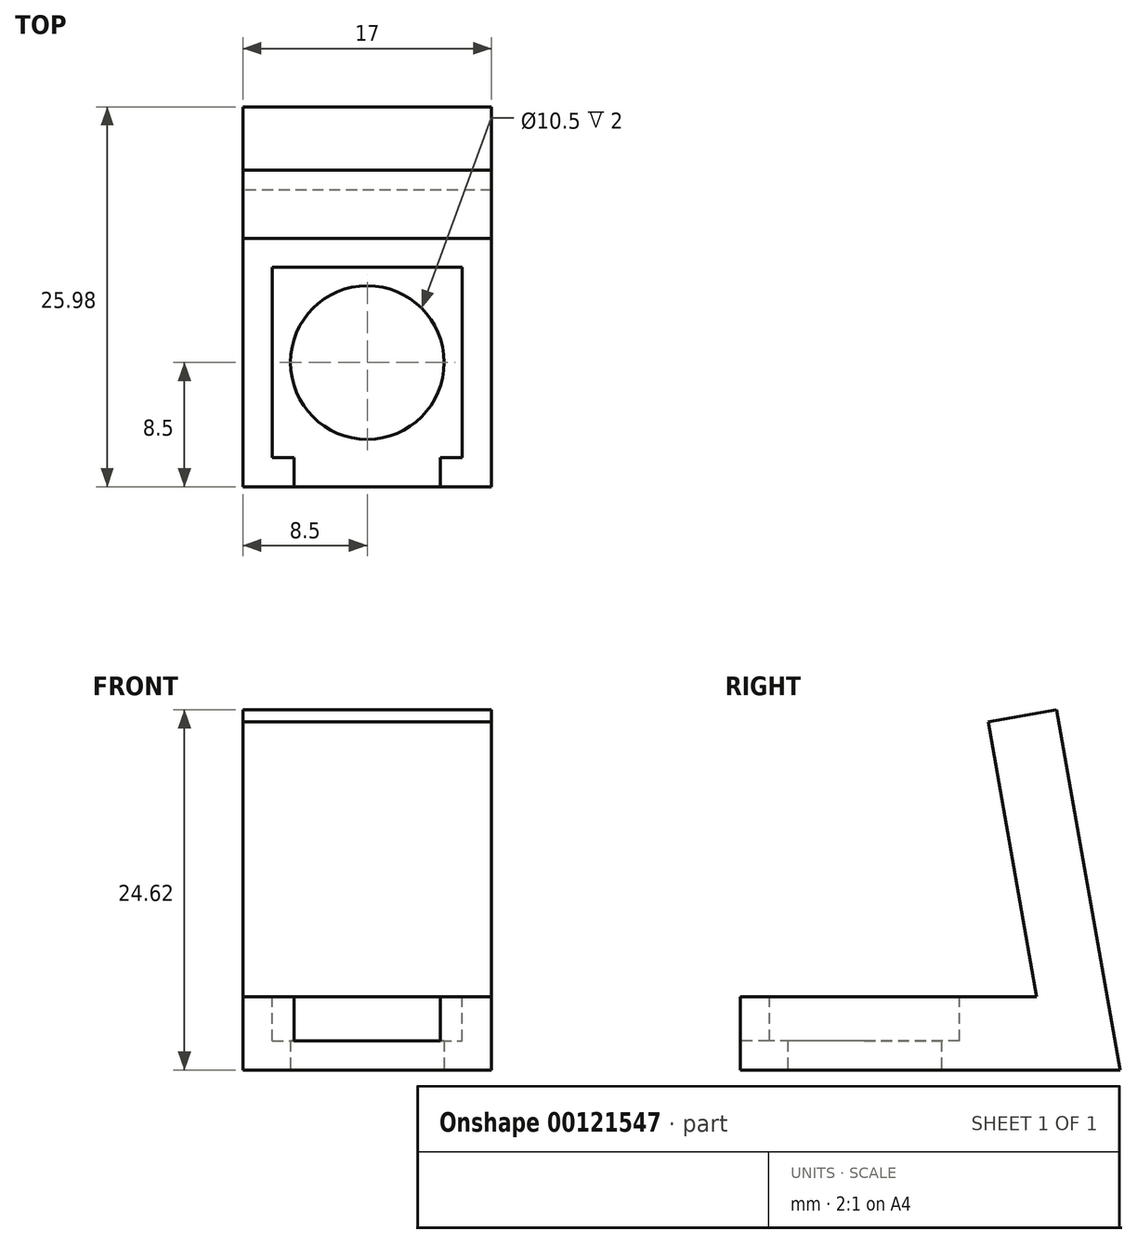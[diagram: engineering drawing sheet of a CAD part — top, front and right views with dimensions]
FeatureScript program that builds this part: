
annotation { "Feature Type Name" : "Feature", "Feature Type Description" : "" }
export const myFeature = defineFeature(function(context is Context, id is Id, definition is map)
    precondition{}
    {
        {
            var Q0;
            Q0=qCreatedBy(makeId("Top.planeOp"),FACE);
            var sketch = newSketch(context, id + "F0", { "sketchPlane" : qUnion([Q0])});
            skLineSegment(sketch, "E0.bottom", {"start": v(-8.5, 8.5) * mm, "end": v(8.5, 8.5) * mm});
            skLineSegment(sketch, "E0.top", {"start": v(-8.5, -8.5) * mm, "end": v(8.5, -8.5) * mm});
            skLineSegment(sketch, "E0.left", {"start": v(-8.5, 8.5) * mm, "end": v(-8.5, -8.5) * mm});
            skLineSegment(sketch, "E0.right", {"start": v(8.5, 8.5) * mm, "end": v(8.5, -8.5) * mm});
            skPoint(sketch, "E0.middle", {"position": v(0, 0) * mm});
            skSolve(sketch);
        }
        {
            var Q0;
            Q0=makeQuery(id+"F0.imprint","IMPRINT",FACE,{"disambiguationData":[TD([[makeQuery(id+"F0.imprint","IMPRINT",EDGE,{"derivedFrom":sQuery(id+"F0.wireOp",EDGE,"E0.bottom")}),-1.0]])]});
            extrude(context, id + "F1", {"entities" : qUnion([Q0]), "depth" : 5 * mm});
        }
        {
            var Q0;
            Q0=makeQuery(id+"F1.opExtrude","CAP_FACE",FACE,{"disambiguationData":[OSD([sQuery(id+"F0.wireOp",EDGE,"E0.bottom"),sQuery(id+"F0.wireOp",EDGE,"E0.top"),sQuery(id+"F0.wireOp",EDGE,"E0.left"),sQuery(id+"F0.wireOp",EDGE,"E0.right")])],"isStart":false});
            var sketch = newSketch(context, id + "F2", { "sketchPlane" : qUnion([Q0])});
            skLineSegment(sketch, "E1.bottom", {"start": v(-6.5, 6.5) * mm, "end": v(6.5, 6.5) * mm});
            skLineSegment(sketch, "E1.top", {"start": v(-6.5, -6.5) * mm, "end": v(-5, -6.5) * mm});
            skLineSegment(sketch, "E1.left", {"start": v(-6.5, 6.5) * mm, "end": v(-6.5, -6.5) * mm});
            skLineSegment(sketch, "E1.right", {"start": v(6.5, 6.5) * mm, "end": v(6.5, -6.5) * mm});
            skPoint(sketch, "E1.middle", {"position": v(0, 0) * mm});
            skLineSegment(sketch, "E2.top", {"start": v(-5, -11.8) * mm, "end": v(5, -11.8) * mm});
            skLineSegment(sketch, "E2.left", {"start": v(-5, -6.5) * mm, "end": v(-5, -11.8) * mm});
            skLineSegment(sketch, "E2.right", {"start": v(5, -6.5) * mm, "end": v(5, -11.8) * mm});
            skLineSegment(sketch, "E3.trimOffspring", {"start": v(5, -6.5) * mm, "end": v(6.5, -6.5) * mm});
            skSolve(sketch);
        }
        {
            var Q0;
            Q0=makeQuery(id+"F2.imprint","IMPRINT",FACE,{"disambiguationData":[TD([[makeQuery(id+"F2.imprint","IMPRINT",EDGE,{"derivedFrom":sQuery(id+"F2.wireOp",EDGE,"E1.bottom")}),-1.0]])]});
            extrude(context, id + "F3", {"entities" : qUnion([Q0]), "operationType" : NewBodyOperationType.REMOVE, "oppositeDirection" : true, "depth" : 3 * mm});
        }
        {
            var Q0;
            Q0=makeQuery(id+"F1.opExtrude","CAP_FACE",FACE,{"disambiguationData":[OSD([sQuery(id+"F0.wireOp",EDGE,"E0.bottom"),sQuery(id+"F0.wireOp",EDGE,"E0.top"),sQuery(id+"F0.wireOp",EDGE,"E0.left"),sQuery(id+"F0.wireOp",EDGE,"E0.right")])],"isStart":true});
            var sketch = newSketch(context, id + "F4", { "sketchPlane" : qUnion([Q0])});
            skCircle(sketch, "E4", {"center": v(0, 0) * mm, "radius": 5.25 * mm});
            skSolve(sketch);
        }
        {
            var Q0;
            Q0=makeQuery(id+"F4.imprint","IMPRINT",FACE,{"disambiguationData":[TD([[makeQuery(id+"F4.imprint","IMPRINT",EDGE,{"derivedFrom":sQuery(id+"F4.wireOp",EDGE,"E4")}),1.0]])]});
            extrude(context, id + "F5", {"entities" : qUnion([Q0]), "operationType" : NewBodyOperationType.REMOVE, "oppositeDirection" : true, "depth" : 25 * mm});
        }
        {
            var Q0;
            Q0=qCreatedBy(makeId("Right.planeOp"),FACE);
            var sketch = newSketch(context, id + "F6", { "sketchPlane" : qUnion([Q0])});
            skLineSegment(sketch, "E5", {"start": v(8.5, 0) * mm, "end": v(17.48, 0) * mm});
            skLineSegment(sketch, "E6", {"start": v(17.48, 0) * mm, "end": v(13.14, 24.62) * mm});
            skLineSegment(sketch, "E7", {"start": v(13.14, 24.62) * mm, "end": v(8.47, 23.8) * mm});
            skLineSegment(sketch, "E8", {"start": v(8.47, 23.8) * mm, "end": v(11.78, 5) * mm});
            skLineSegment(sketch, "E9", {"start": v(11.78, 5) * mm, "end": v(8.5, 5) * mm});
            skLineSegment(sketch, "E10", {"start": v(8.5, 5) * mm, "end": v(8.5, 0) * mm});
            skSolve(sketch);
        }
        {
            var Q0;
            Q0 = qSketchRegion(id + "F6", true);
            var Q1;
            Q1=makeQuery(id+"F6.imprint","IMPRINT",FACE,{"disambiguationData":[TD([[makeQuery(id+"F6.imprint","IMPRINT",EDGE,{"derivedFrom":sQuery(id+"F6.wireOp",EDGE,"E5")}),1.0]])]});
            extrude(context, id + "F7", {"entities" : qUnion([Q0, Q1]), "operationType" : NewBodyOperationType.ADD, "endBound" : BoundingType.SYMMETRIC, "depth" : 17 * mm});
        }
    });
